# Revit family: O5M
name_source: partatom
category: Mechanical Equipment
units: mm (PartAtom-declared; Revit-internal decimal feet)

## family parameters
Always vertical = Yes
Cut with Voids When Loaded = No
OmniClass Number = 23.40.40.11.17
OmniClass Title = Refrigerated Cases
Part Type = Normal
Room Calculation Point = No
Round Connector Dimension = Use Radius
Shared = No
Work Plane-Based = Yes

## types (11) — shared parameters
20" Shelf = Yes
Application Discipline = Deli with 2.5 Extended Sill
BOTTOM ELECTRICAL = Yes
BOTTOM REFRIGERATION PIPING = Yes
BTUH Conventional = 1600
BTUH Parallel = 1458
Certifications = NSF 7, UL471, CSA
DATE = 05/19/2016
DESIGNERS NAME = SHIDDRAMESH
DRAIN PIPING = Yes
Default Elevation = 48"
Defrosts Per Day = 4
Description = Multi-Deck Merchandiser
Discharge Air (°F) = 30 °F
Discharge Air Velocity (FPM) = 270 FPM
EQUIPMENT DESCRIPTION = Multi-Deck Merchandiser
EQUIPMENT MARK = O5M-5BF
Electric Defrost Fail-Safe = 32 (Min)
Electric Defrost Termination Temp (°F) = 47 °F
Evaporator (°F) = 22 °F
FLAT FRONT = Yes
GLASS = Glass
Height = 81 5/8"
High Efficiency Amps = 1 A
High Power (Cornice) Amps = 0 A
Hot Gas Defrost Fail-Safe = 26 (Min)
Hot Gas Defrost Termination Temp (°F) = 45 °F
Item Description = Multi-Deck Merchandiser
LIGHT MATERIAL = GALVANIZED STEEL
Legend Number = O5M-5BF
Manufacturer = HILL PHOENIX
Model = O5M-5BF
PAINTED METAL UPPER SHELF = PAINTED SHELVES
REAR REFRIGERATION PIPING = Yes
REFRIGERATION PIPING = COPPER PIPE
Refgn = 28 5/8"
Run-Off Time (Min) = 6-8 (Min)
STAINLESS STEEL = GALVANIZED STEEL
Standard Power Amps = 0 A
Superheat Set Point @ Bulb (°F) = 6-8 °F
TOP ELECTRICAL = Yes
TOP REFRIGERATION PIPING = Yes
TRIM MATERIAL = creme
Timed-Off Defrost Fail-Safe (Min) = 42 (Min)
Timed-Off Defrost Termination Temp = 47 °F
URL = http://www.hillphoenix.com
Width = 43 1/4"
origin 2 front = Yes

## per-type parameters (varying)
| type | CASE MAIN | CENTER LINE | CURVED CORNER WITH NIGHT COVER | CURVED CORNICE | DRAIN LINE | FACETED CORNICE | FACETED CORNICE WITH NIGHT COVER | FLAT CORNICE WITH NIGHT COVER | High Efficiency Watts | High Power (Cornice) Watts | Length | Length of Cases | Light Length | Lights Per Row | Number of Fans | Standard Power Watts | classic 2 metal front | classic 2 polymer | creme | flat front angled top | flat front flat top | red |
| 06' | Yes | 36" | Yes | Yes | 36" | Yes | Yes | Yes | 70 W | 30 W | 72" | 72" | 3' | 2 | 4 | 17 W | Yes | Yes | BLACK PAINTED METAL | Yes | Yes | BLACK |
| 08' | Yes | 48" | Yes | Yes | 48" | Yes | Yes | Yes | 70 W | 43 W | 96" | 96" | 4' | 2 | 4 | 24 W | Yes | Yes | BLACK PAINTED METAL | Yes | Yes | BLACK |
| 12' | Yes | 72" | No | No | 72" | No | No | No | 106 W | 45 W | 144" | 144" | 4' | 3 | 6 | 18 W | No | No | creme | No | No | BLACK PAINTED METAL |
| 8' | Yes | 48" | Yes | Yes | 48" | Yes | Yes | Yes | 70 W | 30 W | 96" | 48" | 4' | 2 | 4 | 12 W | Yes | Yes | BLACK PAINTED METAL | Yes | Yes | BLACK |
| 6' | Yes | 36" | Yes | Yes | 36" | Yes | Yes | Yes | 70 W | 24 W | 72" | 48" | 3' | 2 | 4 | 9 W | Yes | Yes | BLACK PAINTED METAL | Yes | Yes | BLACK |
| 04' | Yes | 24" | Yes | Yes | 36" | Yes | Yes | Yes | 70 W | 30 W | 48" | 72" | 3' | 2 | 4 | 17 W | Yes | Yes | BLACK PAINTED METAL | Yes | Yes | BLACK |
| 4' | Yes | 24" | Yes | Yes | 36" | Yes | Yes | Yes | 70 W | 30 W | 48" | 72" | 3' | 2 | 4 | 17 W | Yes | Yes | BLACK PAINTED METAL | Yes | Yes | BLACK |
| OS 45 WEDGE LEFT | No | 36" | Yes | Yes | 36" | Yes | Yes | Yes | 70 W | 24 W | 72" | 48" | 3' | 2 | 4 | 9 W | Yes | Yes | BLACK PAINTED METAL | Yes | Yes | BLACK |
| OS 45 WEDGE RIGHT | No | 36" | Yes | Yes | 36" | Yes | Yes | Yes | 70 W | 24 W | 72" | 48" | 3' | 2 | 4 | 9 W | Yes | Yes | BLACK PAINTED METAL | Yes | Yes | BLACK |
| IS 45 WEDGE LEFT | No | 36" | Yes | Yes | 36" | Yes | Yes | Yes | 70 W | 24 W | 72" | 48" | 3' | 2 | 4 | 9 W | Yes | Yes | BLACK PAINTED METAL | Yes | Yes | BLACK |
| IS 45 WEDGE RIGHT | No | 36" | Yes | Yes | 36" | Yes | Yes | Yes | 70 W | 24 W | 72" | 48" | 3' | 2 | 4 | 9 W | Yes | Yes | BLACK PAINTED METAL | Yes | Yes | BLACK |

## geometry (parser evidence)
native form markers: Blend x17, Sweep x11
no freeform markers — native parametric forms only
